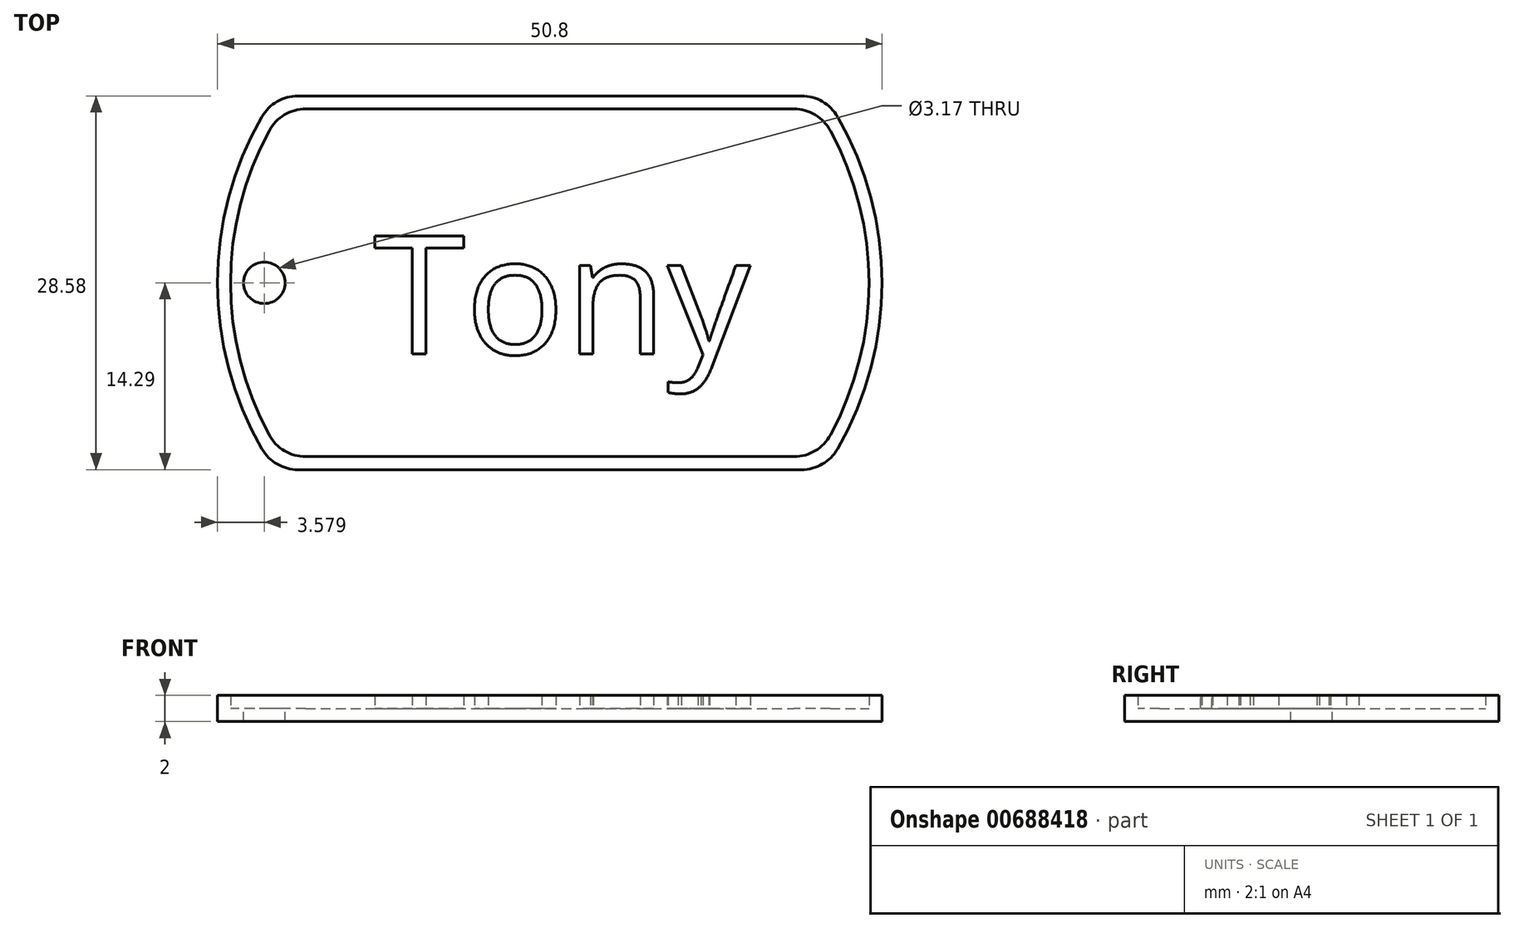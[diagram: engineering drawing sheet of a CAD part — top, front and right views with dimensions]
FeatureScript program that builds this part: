
annotation { "Feature Type Name" : "Feature", "Feature Type Description" : "" }
export const myFeature = defineFeature(function(context is Context, id is Id, definition is map)
    precondition{}
    {
        {
            var Q0;
            Q0=qCreatedBy(makeId("Top.planeOp"),FACE);
            var sketch = newSketch(context, id + "F0", { "sketchPlane" : qUnion([Q0])});
            skArc(sketch, "E0", {"start": v(-22, 12.7) * mm, "mid": v(-25.4, 0) * mm, "end": v(-22, -12.7) * mm});
            skLineSegment(sketch, "E1.top", {"start": v(-19.25, -14.29) * mm, "end": v(19.25, -14.29) * mm});
            skArc(sketch, "E2.trimOffspring", {"start": v(22, -12.7) * mm, "mid": v(25.4, 0) * mm, "end": v(22, 12.7) * mm});
            skLineSegment(sketch, "E3", {"start": v(-19.25, 14.29) * mm, "end": v(19.25, 14.29) * mm});
            skPoint(sketch, "E4.visualSharp", {"position": v(-21, 14.29) * mm});
            skArc(sketch, "E4.filletArc", {"start": v(-19.25, 14.29) * mm, "mid": v(-20.83, 13.86) * mm, "end": v(-22, 12.7) * mm});
            skPoint(sketch, "E5.visualSharp", {"position": v(21, 14.29) * mm});
            skArc(sketch, "E5.filletArc", {"start": v(22, 12.7) * mm, "mid": v(20.83, 13.86) * mm, "end": v(19.25, 14.29) * mm});
            skPoint(sketch, "E6.visualSharp", {"position": v(21, -14.29) * mm});
            skArc(sketch, "E6.filletArc", {"start": v(19.25, -14.29) * mm, "mid": v(20.83, -13.86) * mm, "end": v(22, -12.7) * mm});
            skPoint(sketch, "E7.visualSharp", {"position": v(-21, -14.29) * mm});
            skArc(sketch, "E7.filletArc", {"start": v(-22, -12.7) * mm, "mid": v(-20.83, -13.86) * mm, "end": v(-19.25, -14.29) * mm});
            skSolve(sketch);
        }
        {
            var Q0;
            Q0=makeQuery(id+"F0.imprint","IMPRINT",FACE,{"disambiguationData":[TD([[makeQuery(id+"F0.imprint","IMPRINT",EDGE,{"derivedFrom":sQuery(id+"F0.wireOp",EDGE,"E0")}),1.0]])]});
            extrude(context, id + "F1", {"entities" : qUnion([Q0]), "depth" : 1 * mm, "offsetDistance" : 25.4 * mm});
        }
        {
            var Q0;
            Q0=makeQuery(id+"F1.opExtrude","CAP_FACE",FACE,{"disambiguationData":[OSD([sQuery(id+"F0.wireOp",EDGE,"E0"),sQuery(id+"F0.wireOp",EDGE,"E1.top"),sQuery(id+"F0.wireOp",EDGE,"E2.trimOffspring"),sQuery(id+"F0.wireOp",EDGE,"E3"),sQuery(id+"F0.wireOp",EDGE,"E4.filletArc"),sQuery(id+"F0.wireOp",EDGE,"E5.filletArc"),sQuery(id+"F0.wireOp",EDGE,"E6.filletArc"),sQuery(id+"F0.wireOp",EDGE,"E7.filletArc")])],"isStart":false});
            var sketch = newSketch(context, id + "F2", { "sketchPlane" : qUnion([Q0])});
            skLineSegment(sketch, "E8.0", {"start": v(-18.66, 13.29) * mm, "end": v(18.66, 13.29) * mm});
            skArc(sketch, "E8.1", {"start": v(-21.45, 11.63) * mm, "mid": v(-24.4, 0) * mm, "end": v(-21.45, -11.63) * mm});
            skLineSegment(sketch, "E8.2", {"start": v(-18.66, -13.29) * mm, "end": v(18.66, -13.29) * mm});
            skArc(sketch, "E8.3", {"start": v(21.45, -11.63) * mm, "mid": v(24.4, 0) * mm, "end": v(21.45, 11.63) * mm});
            skPoint(sketch, "E9.visualSharp", {"position": v(-20.46, 13.29) * mm});
            skArc(sketch, "E9.filletArc", {"start": v(-18.66, 13.29) * mm, "mid": v(-20.29, 12.84) * mm, "end": v(-21.45, 11.63) * mm});
            skPoint(sketch, "E10.visualSharp", {"position": v(20.46, 13.29) * mm});
            skArc(sketch, "E10.filletArc", {"start": v(21.45, 11.63) * mm, "mid": v(20.29, 12.84) * mm, "end": v(18.66, 13.29) * mm});
            skPoint(sketch, "E11.visualSharp", {"position": v(20.46, -13.29) * mm});
            skArc(sketch, "E11.filletArc", {"start": v(18.66, -13.29) * mm, "mid": v(20.29, -12.84) * mm, "end": v(21.45, -11.63) * mm});
            skPoint(sketch, "E12.visualSharp", {"position": v(-20.46, -13.29) * mm});
            skArc(sketch, "E12.filletArc", {"start": v(-21.45, -11.63) * mm, "mid": v(-20.29, -12.84) * mm, "end": v(-18.66, -13.29) * mm});
            skLineSegment(sketch, "E13.0", {"start": v(-19.25, 14.29) * mm, "end": v(19.25, 14.29) * mm});
            skArc(sketch, "E13.1", {"start": v(-22, 12.7) * mm, "mid": v(-25.4, 0) * mm, "end": v(-22, -12.7) * mm});
            skLineSegment(sketch, "E13.2", {"start": v(-19.25, -14.29) * mm, "end": v(19.25, -14.29) * mm});
            skArc(sketch, "E13.3", {"start": v(22, -12.7) * mm, "mid": v(25.4, 0) * mm, "end": v(22, 12.7) * mm});
            skPoint(sketch, "E14.visualSharp", {"position": v(-21, -14.29) * mm});
            skArc(sketch, "E14.filletArc", {"start": v(-22, -12.7) * mm, "mid": v(-20.83, -13.86) * mm, "end": v(-19.25, -14.29) * mm});
            skPoint(sketch, "E15.visualSharp", {"position": v(21, -14.29) * mm});
            skArc(sketch, "E15.filletArc", {"start": v(19.25, -14.29) * mm, "mid": v(20.83, -13.86) * mm, "end": v(22, -12.7) * mm});
            skPoint(sketch, "E16.visualSharp", {"position": v(21, 14.29) * mm});
            skArc(sketch, "E16.filletArc", {"start": v(22, 12.7) * mm, "mid": v(20.83, 13.86) * mm, "end": v(19.25, 14.29) * mm});
            skPoint(sketch, "E17.visualSharp", {"position": v(-21, 14.29) * mm});
            skArc(sketch, "E17.filletArc", {"start": v(-19.25, 14.29) * mm, "mid": v(-20.83, 13.86) * mm, "end": v(-22, 12.7) * mm});
            skSolve(sketch);
        }
        {
            var Q0;
            Q0=makeQuery(id+"F2.imprint","IMPRINT",FACE,{"disambiguationData":[TD([[makeQuery(id+"F2.imprint","IMPRINT",EDGE,{"derivedFrom":sQuery(id+"F2.wireOp",EDGE,"E8.0")}),1.0]])]});
            extrude(context, id + "F3", {"entities" : qUnion([Q0]), "operationType" : NewBodyOperationType.ADD, "depth" : 1 * mm, "offsetDistance" : 25.4 * mm});
        }
        {
            var Q0;
            Q0=makeQuery(id+"F1.opExtrude","CAP_FACE",FACE,{"disambiguationData":[OSD([sQuery(id+"F0.wireOp",EDGE,"E0"),sQuery(id+"F0.wireOp",EDGE,"E1.top"),sQuery(id+"F0.wireOp",EDGE,"E2.trimOffspring"),sQuery(id+"F0.wireOp",EDGE,"E3"),sQuery(id+"F0.wireOp",EDGE,"E4.filletArc"),sQuery(id+"F0.wireOp",EDGE,"E5.filletArc"),sQuery(id+"F0.wireOp",EDGE,"E6.filletArc"),sQuery(id+"F0.wireOp",EDGE,"E7.filletArc")])],"isStart":false});
            var sketch = newSketch(context, id + "F4", { "sketchPlane" : qUnion([Q0])});
            skCircle(sketch, "E18", {"center": v(-21.82, 0) * mm, "radius": 1.59 * mm});
            skSolve(sketch);
        }
        {
            var Q0;
            Q0=makeQuery(id+"F4.imprint","IMPRINT",FACE,{"disambiguationData":[TD([[makeQuery(id+"F4.imprint","IMPRINT",EDGE,{"derivedFrom":sQuery(id+"F4.wireOp",EDGE,"E18")}),1.0]])]});
            extrude(context, id + "F5", {"entities" : qUnion([Q0]), "operationType" : NewBodyOperationType.REMOVE, "oppositeDirection" : true, "depth" : 1 * mm, "offsetDistance" : 25.4 * mm});
        }
        {
            var Q0;
            Q0=makeQuery(id+"F2.imprint","IMPRINT",FACE,{"disambiguationData":[TD([[makeQuery(id+"F2.imprint","IMPRINT",EDGE,{"derivedFrom":sQuery(id+"F2.wireOp",EDGE,"E8.0")}),-1.0]])]});
            var sketch = newSketch(context, id + "F6", { "sketchPlane" : qUnion([Q0])});
            skText(sketch, "E19", { "text": "Tony", "fontName": "OpenSans-Regular.ttf"});
            const initialGuessF6  = {"E19": [-0.01348, -0.00545, 1, 0, 0.00912]};
            skSetInitialGuess(sketch, initialGuessF6);
            skSolve(sketch);
        }
        {
            var Q0;
            Q0 = qSketchRegion(id + "F6", true);
            extrude(context, id + "F7", {"entities" : qUnion([Q0]), "operationType" : NewBodyOperationType.ADD, "depth" : 1 * mm, "offsetDistance" : 25.4 * mm});
        }
    });
